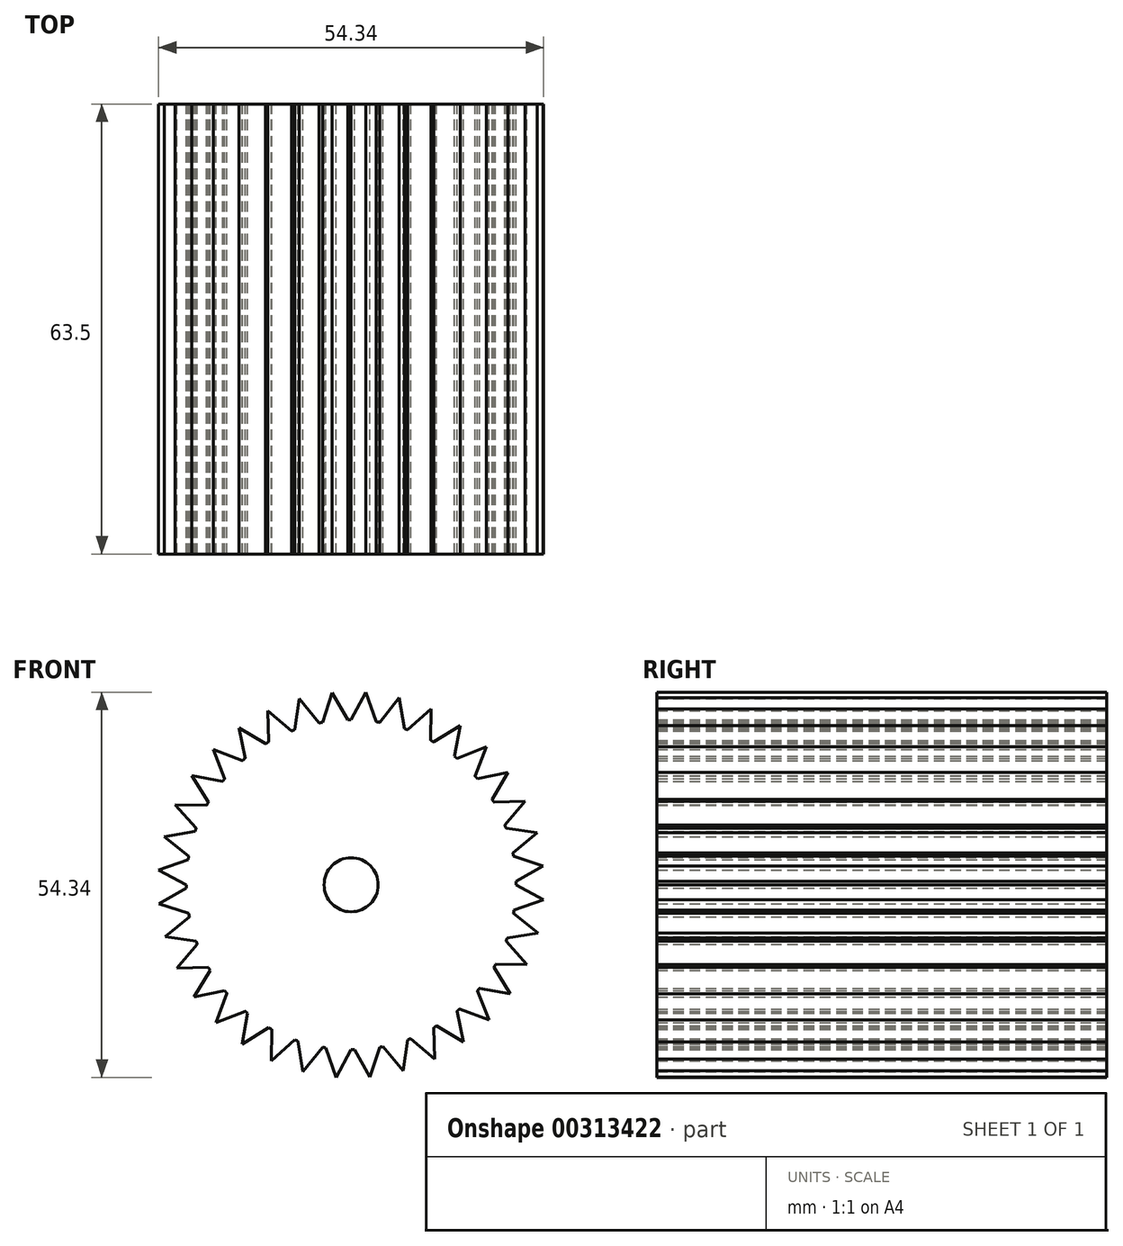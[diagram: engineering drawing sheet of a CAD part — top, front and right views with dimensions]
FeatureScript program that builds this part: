
annotation { "Feature Type Name" : "Feature", "Feature Type Description" : "" }
export const myFeature = defineFeature(function(context is Context, id is Id, definition is map)
    precondition{}
    {
        {
            var Q0;
            Q0=qCreatedBy(makeId("Front.planeOp"),FACE);
            var sketch = newSketch(context, id + "F0", { "sketchPlane" : qUnion([Q0])});
            skCircle(sketch, "E0", {"center": v(0, 0) * mm, "radius": 23.28 * mm});
            skPoint(sketch, "E1.visualSharp", {"position": v(-13.38, 28.48) * mm});
            skPoint(sketch, "E2.visualSharp", {"position": v(-14.6, 28.16) * mm});
            skLineSegment(sketch, "E3", {"start": v(-10.49, 20.78) * mm, "end": v(-10.49, 20.78) * mm});
            skLineSegment(sketch, "E4", {"start": v(0, 23.28) * mm, "end": v(2.1, 27.17) * mm});
            skLineSegment(sketch, "E5", {"start": v(2.1, 27.17) * mm, "end": v(3.57, 23) * mm});
            skLineSegment(sketch, "E6", {"start": v(3.57, 23) * mm, "end": v(0, 23.28) * mm});
            skLineSegment(sketch, "E7.1.0", {"start": v(-4.04, 22.93) * mm, "end": v(-2.65, 27.12) * mm});
            skLineSegment(sketch, "E7.1.1", {"start": v(-2.65, 27.12) * mm, "end": v(-0.48, 23.27) * mm});
            skLineSegment(sketch, "E7.1.2", {"start": v(-0.48, 23.27) * mm, "end": v(-4.04, 22.93) * mm});
            skLineSegment(sketch, "E7.2.0", {"start": v(-7.96, 21.88) * mm, "end": v(-7.32, 26.25) * mm});
            skLineSegment(sketch, "E7.2.1", {"start": v(-7.32, 26.25) * mm, "end": v(-4.51, 22.84) * mm});
            skLineSegment(sketch, "E7.2.2", {"start": v(-4.51, 22.84) * mm, "end": v(-7.96, 21.88) * mm});
            skLineSegment(sketch, "E7.3.0", {"start": v(-11.64, 20.16) * mm, "end": v(-11.77, 24.58) * mm});
            skLineSegment(sketch, "E7.3.1", {"start": v(-11.77, 24.58) * mm, "end": v(-8.4, 21.7) * mm});
            skLineSegment(sketch, "E7.3.2", {"start": v(-8.4, 21.7) * mm, "end": v(-11.64, 20.16) * mm});
            skLineSegment(sketch, "E7.4.0", {"start": v(-14.96, 17.83) * mm, "end": v(-15.86, 22.16) * mm});
            skLineSegment(sketch, "E7.4.1", {"start": v(-15.86, 22.16) * mm, "end": v(-12.05, 19.92) * mm});
            skLineSegment(sketch, "E7.4.2", {"start": v(-12.05, 19.92) * mm, "end": v(-14.96, 17.83) * mm});
            skLineSegment(sketch, "E7.5.0", {"start": v(-17.83, 14.96) * mm, "end": v(-19.47, 19.07) * mm});
            skLineSegment(sketch, "E7.5.1", {"start": v(-19.47, 19.07) * mm, "end": v(-15.33, 17.52) * mm});
            skLineSegment(sketch, "E7.5.2", {"start": v(-15.33, 17.52) * mm, "end": v(-17.83, 14.96) * mm});
            skLineSegment(sketch, "E7.6.0", {"start": v(-20.16, 11.64) * mm, "end": v(-22.48, 15.4) * mm});
            skLineSegment(sketch, "E7.6.1", {"start": v(-22.48, 15.4) * mm, "end": v(-18.14, 14.6) * mm});
            skLineSegment(sketch, "E7.6.2", {"start": v(-18.14, 14.6) * mm, "end": v(-20.16, 11.64) * mm});
            skLineSegment(sketch, "E7.7.0", {"start": v(-21.88, 7.96) * mm, "end": v(-24.81, 11.26) * mm});
            skLineSegment(sketch, "E7.7.1", {"start": v(-24.81, 11.26) * mm, "end": v(-20.4, 11.22) * mm});
            skLineSegment(sketch, "E7.7.2", {"start": v(-20.4, 11.22) * mm, "end": v(-21.88, 7.96) * mm});
            skLineSegment(sketch, "E7.8.0", {"start": v(-22.93, 4.04) * mm, "end": v(-26.4, 6.78) * mm});
            skLineSegment(sketch, "E7.8.1", {"start": v(-26.4, 6.78) * mm, "end": v(-22.03, 7.51) * mm});
            skLineSegment(sketch, "E7.8.2", {"start": v(-22.03, 7.51) * mm, "end": v(-22.93, 4.04) * mm});
            skLineSegment(sketch, "E7.9.0", {"start": v(-23.28, 0) * mm, "end": v(-27.17, 2.1) * mm});
            skLineSegment(sketch, "E7.9.1", {"start": v(-27.17, 2.1) * mm, "end": v(-23, 3.57) * mm});
            skLineSegment(sketch, "E7.9.2", {"start": v(-23, 3.57) * mm, "end": v(-23.28, 0) * mm});
            skLineSegment(sketch, "E7.10.0", {"start": v(-22.93, -4.04) * mm, "end": v(-27.12, -2.65) * mm});
            skLineSegment(sketch, "E7.10.1", {"start": v(-27.12, -2.65) * mm, "end": v(-23.27, -0.48) * mm});
            skLineSegment(sketch, "E7.10.2", {"start": v(-23.27, -0.48) * mm, "end": v(-22.93, -4.04) * mm});
            skLineSegment(sketch, "E7.11.0", {"start": v(-21.88, -7.96) * mm, "end": v(-26.25, -7.32) * mm});
            skLineSegment(sketch, "E7.11.1", {"start": v(-26.25, -7.32) * mm, "end": v(-22.84, -4.51) * mm});
            skLineSegment(sketch, "E7.11.2", {"start": v(-22.84, -4.51) * mm, "end": v(-21.88, -7.96) * mm});
            skLineSegment(sketch, "E7.12.0", {"start": v(-20.16, -11.64) * mm, "end": v(-24.58, -11.77) * mm});
            skLineSegment(sketch, "E7.12.1", {"start": v(-24.58, -11.77) * mm, "end": v(-21.7, -8.4) * mm});
            skLineSegment(sketch, "E7.12.2", {"start": v(-21.7, -8.4) * mm, "end": v(-20.16, -11.64) * mm});
            skLineSegment(sketch, "E7.13.0", {"start": v(-17.83, -14.96) * mm, "end": v(-22.16, -15.86) * mm});
            skLineSegment(sketch, "E7.13.1", {"start": v(-22.16, -15.86) * mm, "end": v(-19.92, -12.05) * mm});
            skLineSegment(sketch, "E7.13.2", {"start": v(-19.92, -12.05) * mm, "end": v(-17.83, -14.96) * mm});
            skLineSegment(sketch, "E7.14.0", {"start": v(-14.96, -17.83) * mm, "end": v(-19.07, -19.47) * mm});
            skLineSegment(sketch, "E7.14.1", {"start": v(-19.07, -19.47) * mm, "end": v(-17.52, -15.33) * mm});
            skLineSegment(sketch, "E7.14.2", {"start": v(-17.52, -15.33) * mm, "end": v(-14.96, -17.83) * mm});
            skLineSegment(sketch, "E7.15.0", {"start": v(-11.64, -20.16) * mm, "end": v(-15.4, -22.48) * mm});
            skLineSegment(sketch, "E7.15.1", {"start": v(-15.4, -22.48) * mm, "end": v(-14.6, -18.14) * mm});
            skLineSegment(sketch, "E7.15.2", {"start": v(-14.6, -18.14) * mm, "end": v(-11.64, -20.16) * mm});
            skLineSegment(sketch, "E7.16.0", {"start": v(-7.96, -21.88) * mm, "end": v(-11.26, -24.81) * mm});
            skLineSegment(sketch, "E7.16.1", {"start": v(-11.26, -24.81) * mm, "end": v(-11.22, -20.4) * mm});
            skLineSegment(sketch, "E7.16.2", {"start": v(-11.22, -20.4) * mm, "end": v(-7.96, -21.88) * mm});
            skLineSegment(sketch, "E7.17.0", {"start": v(-4.04, -22.93) * mm, "end": v(-6.78, -26.4) * mm});
            skLineSegment(sketch, "E7.17.1", {"start": v(-6.78, -26.4) * mm, "end": v(-7.51, -22.03) * mm});
            skLineSegment(sketch, "E7.17.2", {"start": v(-7.51, -22.03) * mm, "end": v(-4.04, -22.93) * mm});
            skLineSegment(sketch, "E8.1.18.0", {"start": v(0, -23.28) * mm, "end": v(-2.1, -27.17) * mm});
            skLineSegment(sketch, "E8.3.18.0", {"start": v(-2.1, -27.17) * mm, "end": v(-3.57, -23) * mm});
            skLineSegment(sketch, "E8.6.18.0", {"start": v(-3.57, -23) * mm, "end": v(0, -23.28) * mm});
            skLineSegment(sketch, "E8.1.19.0", {"start": v(4.04, -22.93) * mm, "end": v(2.65, -27.12) * mm});
            skLineSegment(sketch, "E8.3.19.0", {"start": v(2.65, -27.12) * mm, "end": v(0.48, -23.27) * mm});
            skLineSegment(sketch, "E8.6.19.0", {"start": v(0.48, -23.27) * mm, "end": v(4.04, -22.93) * mm});
            skLineSegment(sketch, "E8.1.20.0", {"start": v(7.96, -21.88) * mm, "end": v(7.32, -26.25) * mm});
            skLineSegment(sketch, "E8.3.20.0", {"start": v(7.32, -26.25) * mm, "end": v(4.51, -22.84) * mm});
            skLineSegment(sketch, "E8.6.20.0", {"start": v(4.51, -22.84) * mm, "end": v(7.96, -21.88) * mm});
            skLineSegment(sketch, "E8.1.21.0", {"start": v(11.64, -20.16) * mm, "end": v(11.77, -24.58) * mm});
            skLineSegment(sketch, "E8.3.21.0", {"start": v(11.77, -24.58) * mm, "end": v(8.4, -21.7) * mm});
            skLineSegment(sketch, "E8.6.21.0", {"start": v(8.4, -21.7) * mm, "end": v(11.64, -20.16) * mm});
            skLineSegment(sketch, "E8.1.22.0", {"start": v(14.96, -17.83) * mm, "end": v(15.86, -22.16) * mm});
            skLineSegment(sketch, "E8.3.22.0", {"start": v(15.86, -22.16) * mm, "end": v(12.05, -19.92) * mm});
            skLineSegment(sketch, "E8.6.22.0", {"start": v(12.05, -19.92) * mm, "end": v(14.96, -17.83) * mm});
            skLineSegment(sketch, "E8.1.23.0", {"start": v(17.83, -14.96) * mm, "end": v(19.47, -19.07) * mm});
            skLineSegment(sketch, "E8.3.23.0", {"start": v(19.47, -19.07) * mm, "end": v(15.33, -17.52) * mm});
            skLineSegment(sketch, "E8.6.23.0", {"start": v(15.33, -17.52) * mm, "end": v(17.83, -14.96) * mm});
            skLineSegment(sketch, "E8.1.24.0", {"start": v(20.16, -11.64) * mm, "end": v(22.48, -15.4) * mm});
            skLineSegment(sketch, "E8.3.24.0", {"start": v(22.48, -15.4) * mm, "end": v(18.14, -14.6) * mm});
            skLineSegment(sketch, "E8.6.24.0", {"start": v(18.14, -14.6) * mm, "end": v(20.16, -11.64) * mm});
            skLineSegment(sketch, "E8.1.25.0", {"start": v(21.88, -7.96) * mm, "end": v(24.81, -11.26) * mm});
            skLineSegment(sketch, "E8.3.25.0", {"start": v(24.81, -11.26) * mm, "end": v(20.4, -11.22) * mm});
            skLineSegment(sketch, "E8.6.25.0", {"start": v(20.4, -11.22) * mm, "end": v(21.88, -7.96) * mm});
            skLineSegment(sketch, "E8.1.26.0", {"start": v(22.93, -4.04) * mm, "end": v(26.4, -6.78) * mm});
            skLineSegment(sketch, "E8.3.26.0", {"start": v(26.4, -6.78) * mm, "end": v(22.03, -7.51) * mm});
            skLineSegment(sketch, "E8.6.26.0", {"start": v(22.03, -7.51) * mm, "end": v(22.93, -4.04) * mm});
            skLineSegment(sketch, "E8.1.27.0", {"start": v(23.28, 0) * mm, "end": v(27.17, -2.1) * mm});
            skLineSegment(sketch, "E8.3.27.0", {"start": v(27.17, -2.1) * mm, "end": v(23, -3.57) * mm});
            skLineSegment(sketch, "E8.6.27.0", {"start": v(23, -3.57) * mm, "end": v(23.28, 0) * mm});
            skLineSegment(sketch, "E8.1.28.0", {"start": v(22.93, 4.04) * mm, "end": v(27.12, 2.65) * mm});
            skLineSegment(sketch, "E8.3.28.0", {"start": v(27.12, 2.65) * mm, "end": v(23.27, 0.48) * mm});
            skLineSegment(sketch, "E8.6.28.0", {"start": v(23.27, 0.48) * mm, "end": v(22.93, 4.04) * mm});
            skLineSegment(sketch, "E8.1.29.0", {"start": v(21.88, 7.96) * mm, "end": v(26.25, 7.32) * mm});
            skLineSegment(sketch, "E8.3.29.0", {"start": v(26.25, 7.32) * mm, "end": v(22.84, 4.51) * mm});
            skLineSegment(sketch, "E8.6.29.0", {"start": v(22.84, 4.51) * mm, "end": v(21.88, 7.96) * mm});
            skLineSegment(sketch, "E8.1.30.0", {"start": v(20.16, 11.64) * mm, "end": v(24.58, 11.77) * mm});
            skLineSegment(sketch, "E8.3.30.0", {"start": v(24.58, 11.77) * mm, "end": v(21.7, 8.4) * mm});
            skLineSegment(sketch, "E8.6.30.0", {"start": v(21.7, 8.4) * mm, "end": v(20.16, 11.64) * mm});
            skLineSegment(sketch, "E8.1.31.0", {"start": v(17.83, 14.96) * mm, "end": v(22.16, 15.86) * mm});
            skLineSegment(sketch, "E8.3.31.0", {"start": v(22.16, 15.86) * mm, "end": v(19.92, 12.05) * mm});
            skLineSegment(sketch, "E8.6.31.0", {"start": v(19.92, 12.05) * mm, "end": v(17.83, 14.96) * mm});
            skLineSegment(sketch, "E8.1.32.0", {"start": v(14.96, 17.83) * mm, "end": v(19.07, 19.47) * mm});
            skLineSegment(sketch, "E8.3.32.0", {"start": v(19.07, 19.47) * mm, "end": v(17.52, 15.33) * mm});
            skLineSegment(sketch, "E8.6.32.0", {"start": v(17.52, 15.33) * mm, "end": v(14.96, 17.83) * mm});
            skLineSegment(sketch, "E8.1.33.0", {"start": v(11.64, 20.16) * mm, "end": v(15.4, 22.48) * mm});
            skLineSegment(sketch, "E8.3.33.0", {"start": v(15.4, 22.48) * mm, "end": v(14.6, 18.14) * mm});
            skLineSegment(sketch, "E8.6.33.0", {"start": v(14.6, 18.14) * mm, "end": v(11.64, 20.16) * mm});
            skLineSegment(sketch, "E8.1.34.0", {"start": v(7.96, 21.88) * mm, "end": v(11.26, 24.81) * mm});
            skLineSegment(sketch, "E8.3.34.0", {"start": v(11.26, 24.81) * mm, "end": v(11.22, 20.4) * mm});
            skLineSegment(sketch, "E8.6.34.0", {"start": v(11.22, 20.4) * mm, "end": v(7.96, 21.88) * mm});
            skLineSegment(sketch, "E8.1.35.0", {"start": v(4.04, 22.93) * mm, "end": v(6.78, 26.4) * mm});
            skLineSegment(sketch, "E8.3.35.0", {"start": v(6.78, 26.4) * mm, "end": v(7.51, 22.03) * mm});
            skLineSegment(sketch, "E8.6.35.0", {"start": v(7.51, 22.03) * mm, "end": v(4.04, 22.93) * mm});
            skSolve(sketch);
        }
        {
            var Q0;
            Q0 = qSketchRegion(id + "F0", true);
            extrude(context, id + "F1", {"entities" : qUnion([Q0]), "depth" : 63.5 * mm});
        }
        {
            var Q0;
            Q0=makeQuery(id+"F1.opExtrude","CAP_FACE",FACE,{"disambiguationData":[OSD([sQuery(id+"F0.wireOp",EDGE,"E0"),sQuery(id+"F0.wireOp",EDGE,"E4"),sQuery(id+"F0.wireOp",EDGE,"E5"),sQuery(id+"F0.wireOp",EDGE,"E7.1.0"),sQuery(id+"F0.wireOp",EDGE,"E7.1.1"),sQuery(id+"F0.wireOp",EDGE,"E7.2.0"),sQuery(id+"F0.wireOp",EDGE,"E7.2.1"),sQuery(id+"F0.wireOp",EDGE,"E7.3.0"),sQuery(id+"F0.wireOp",EDGE,"E7.3.1"),sQuery(id+"F0.wireOp",EDGE,"E7.4.0"),sQuery(id+"F0.wireOp",EDGE,"E7.4.1"),sQuery(id+"F0.wireOp",EDGE,"E7.5.0"),sQuery(id+"F0.wireOp",EDGE,"E7.5.1"),sQuery(id+"F0.wireOp",EDGE,"E7.6.0"),sQuery(id+"F0.wireOp",EDGE,"E7.6.1"),sQuery(id+"F0.wireOp",EDGE,"E7.7.0"),sQuery(id+"F0.wireOp",EDGE,"E7.7.1"),sQuery(id+"F0.wireOp",EDGE,"E7.8.0"),sQuery(id+"F0.wireOp",EDGE,"E7.8.1"),sQuery(id+"F0.wireOp",EDGE,"E7.9.0"),sQuery(id+"F0.wireOp",EDGE,"E7.9.1"),sQuery(id+"F0.wireOp",EDGE,"E7.10.0"),sQuery(id+"F0.wireOp",EDGE,"E7.10.1"),sQuery(id+"F0.wireOp",EDGE,"E7.11.0"),sQuery(id+"F0.wireOp",EDGE,"E7.11.1"),sQuery(id+"F0.wireOp",EDGE,"E7.12.0"),sQuery(id+"F0.wireOp",EDGE,"E7.12.1"),sQuery(id+"F0.wireOp",EDGE,"E7.13.0"),sQuery(id+"F0.wireOp",EDGE,"E7.13.1"),sQuery(id+"F0.wireOp",EDGE,"E7.14.0"),sQuery(id+"F0.wireOp",EDGE,"E7.14.1"),sQuery(id+"F0.wireOp",EDGE,"E7.15.0"),sQuery(id+"F0.wireOp",EDGE,"E7.15.1"),sQuery(id+"F0.wireOp",EDGE,"E7.16.0"),sQuery(id+"F0.wireOp",EDGE,"E7.16.1"),sQuery(id+"F0.wireOp",EDGE,"E7.17.0"),sQuery(id+"F0.wireOp",EDGE,"E7.17.1")])],"isStart":false});
            var sketch = newSketch(context, id + "F2", { "sketchPlane" : qUnion([Q0])});
            skCircle(sketch, "E9", {"center": v(0, 0) * mm, "radius": 3.8 * mm});
            skSolve(sketch);
        }
        {
            var Q0;
            Q0 = qSketchRegion(id + "F2", true);
            extrude(context, id + "F3", {"entities" : qUnion([Q0]), "operationType" : NewBodyOperationType.REMOVE, "oppositeDirection" : true, "depth" : 101.6 * mm});
        }
    });
